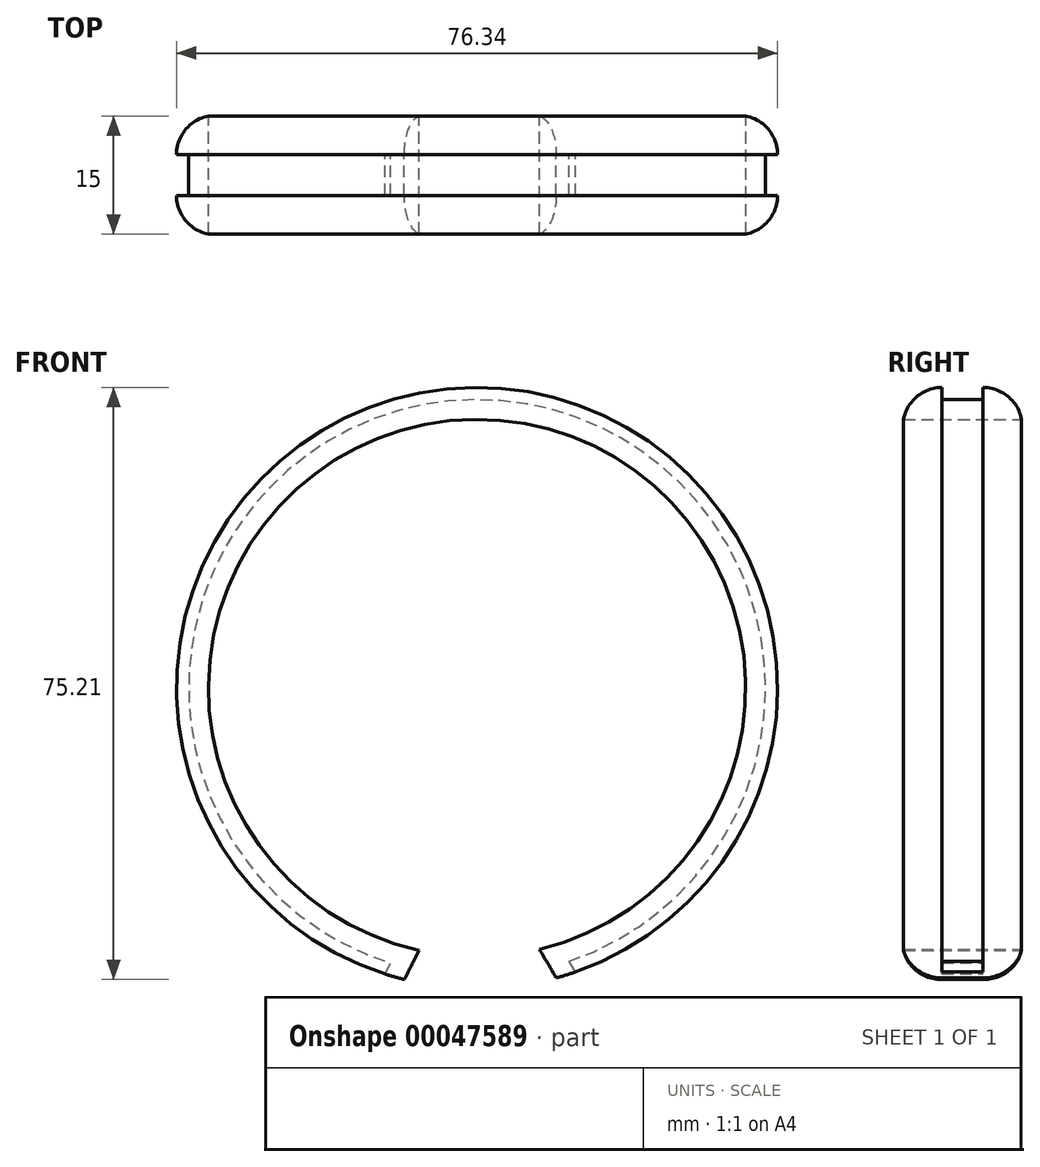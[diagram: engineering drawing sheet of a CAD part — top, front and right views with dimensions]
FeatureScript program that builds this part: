
annotation { "Feature Type Name" : "Feature", "Feature Type Description" : "" }
export const myFeature = defineFeature(function(context is Context, id is Id, definition is map)
    precondition{}
    {
        {
            var Q0;
            Q0=qCreatedBy(makeId("Front.planeOp"),FACE);
            var sketch = newSketch(context, id + "F0", { "sketchPlane" : qUnion([Q0])});
            skCircle(sketch, "E0", {"center": v(0, 0) * mm, "radius": 38.17 * mm});
            skCircle(sketch, "E1", {"center": v(0, 0) * mm, "radius": 34.13 * mm});
            skLineSegment(sketch, "E2", {"start": v(-7.35, -33.33) * mm, "end": v(-9.25, -37.04) * mm});
            skLineSegment(sketch, "E3", {"start": v(7.93, -33.2) * mm, "end": v(10.05, -36.83) * mm});
            skSolve(sketch);
        }
        {
            var Q0;
            {var subQ1=sQuery(id+"F0.wireOp",EDGE,"E2");Q0=makeQuery(id+"F0.imprint","IMPRINT",FACE,{"disambiguationData":[TD([[makeQuery(id+"F0.imprint","IMPRINT",EDGE,{"derivedFrom":subQ1}),-1.0]])]});}
            extrude(context, id + "F1", {"entities" : qUnion([Q0]), "depth" : 15 * mm});
        }
        {
            var Q0;
            Q0=makeQuery(id+"F1.opExtrude","CAP_EDGE",EDGE,{"disambiguationData":[OSD([sQuery(id+"F0.wireOp",EDGE,"E0")])],"isStart":true});
            var Q1;
            Q1=makeQuery(id+"F1.opExtrude","CAP_EDGE",EDGE,{"disambiguationData":[OSD([sQuery(id+"F0.wireOp",EDGE,"E0")])],"isStart":false});
            fillet(context, id + "F2", {"entities" : qUnion([Q0, Q1]), "radius" : 5 * mm, "tangentPropagation" : true, "allowEdgeOverflow" : false});
        }
        {
            var Q0;
            Q0=makeQuery(id+"F1.opExtrude","SWEPT_FACE",FACE,{"disambiguationData":[OSD([sQuery(id+"F0.wireOp",EDGE,"E0")])]});
            shell(context, id + "F3", {"entities" : qUnion([Q0]), "thickness" : 2.5 * mm});
        }
    });
